# Revit family: Cleanout_Floor_Adjustable-Zurn-CO2450
name_source: partatom
category: Plumbing Fixtures
units: mm (PartAtom-declared; Revit-internal decimal feet)

## family parameters
Always vertical = Yes
Cut with Voids When Loaded = No
Maintain Annotation Orientation = No
OmniClass Number = 23.70.50.21.24.14
OmniClass Title = Deck Waste Water Drains
Part Type = Normal
Room Calculation Point = No
Round Connector Dimension = Use Radius
Shared = No
Work Plane-Based = No

## types (6) — shared parameters
Assembly Code = D2030100
CW Connection = No
Default Elevation = 20 "
Description = ADJUSTABLE FLOOR CLEANOUT
HW Connection = No
Manufacturer = Zurn Water, LLC
Manufacurer Brand = Zurn
Model = CO2450
Modified Date = 03/13/2025
Product Documentation Link = https://www.bimobject.com
Product Page URL = https://www.zurn.com
Product data url = https://www.bimobject.com
URL = www.zurn.com
Vent Connection = No
WFU = 1
Waste Connection = Yes
zero-valued in all types: Body Height_E, CWFU, HWFU

## per-type parameters (varying)
| type | B Dimension | Connector Radius | Main Material | Pipe Size_A Inside Diameter | Pipe Size_A Nominal Diameter | Pipe Size_A Outer Diameter |
| CO-2450-PV2 | 1.75 " | 1 " | Polyvinyl Chloride - Zurn - Polished | 2.067 " | 2 " | 2.375 " |
| CO-2450-PV3 | 3 " | 1.5 " | Polyvinyl Chloride - Zurn - Polished | 3.068 " | 3 " | 3.5 " |
| CO-2450-PV4 | 3.438 " | 2 " | Polyvinyl Chloride - Zurn - Polished | 4.026 " | 4 " | 4.5 " |
| CO-2450-AB2 | 1.75 " | 1 " | Acrylonitrile Butadiene Styrene - Zurn - Polished | 2.067 " | 2 " | 2.375 " |
| CO-2450-AB3 | 3 " | 1.5 " | Acrylonitrile Butadiene Styrene - Zurn - Polished | 3.068 " | 3 " | 3.5 " |
| CO-2450-AB4 | 3.438 " | 2 " | Acrylonitrile Butadiene Styrene - Zurn - Polished | 4.026 " | 4 " | 4.5 " |

## geometry (parser evidence)
native form markers: Blend x6, Sweep x3
no freeform markers — native parametric forms only
